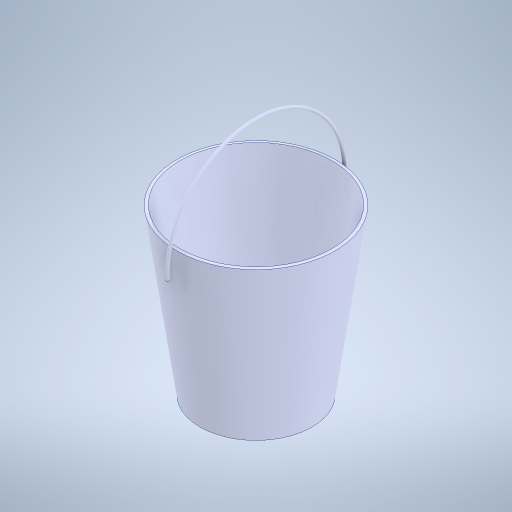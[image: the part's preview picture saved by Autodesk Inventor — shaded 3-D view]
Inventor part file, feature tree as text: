
AUTODESK INVENTOR PART (.ipt)
format: ipt  version: 2023 (Build 270158000, 158)  size: 289,280 bytes
history: native  units: in
note: dims shown in document units (in); Inventor stores cm internally (conversion verified against a paired STEP export)
features: revolve x1, fillet x1
ambient origin geometry x8: Origin, YZ Plane, XZ Plane, XY Plane, X Axis, Y Axis, Z Axis, Center Point
bodies: Solid1 (feature_tree), Solid2 (feature_tree)
feature tree (2):
  revolve  "Revolve1"  [1 undecoded]
  fillet  "Fillet1"  [1 undecoded]
note: 2 required parameter values undecoded (feature->parameter linkage not recoverable at this tier; creation-order binding heuristic only, values carry confidence <= 0.55)
